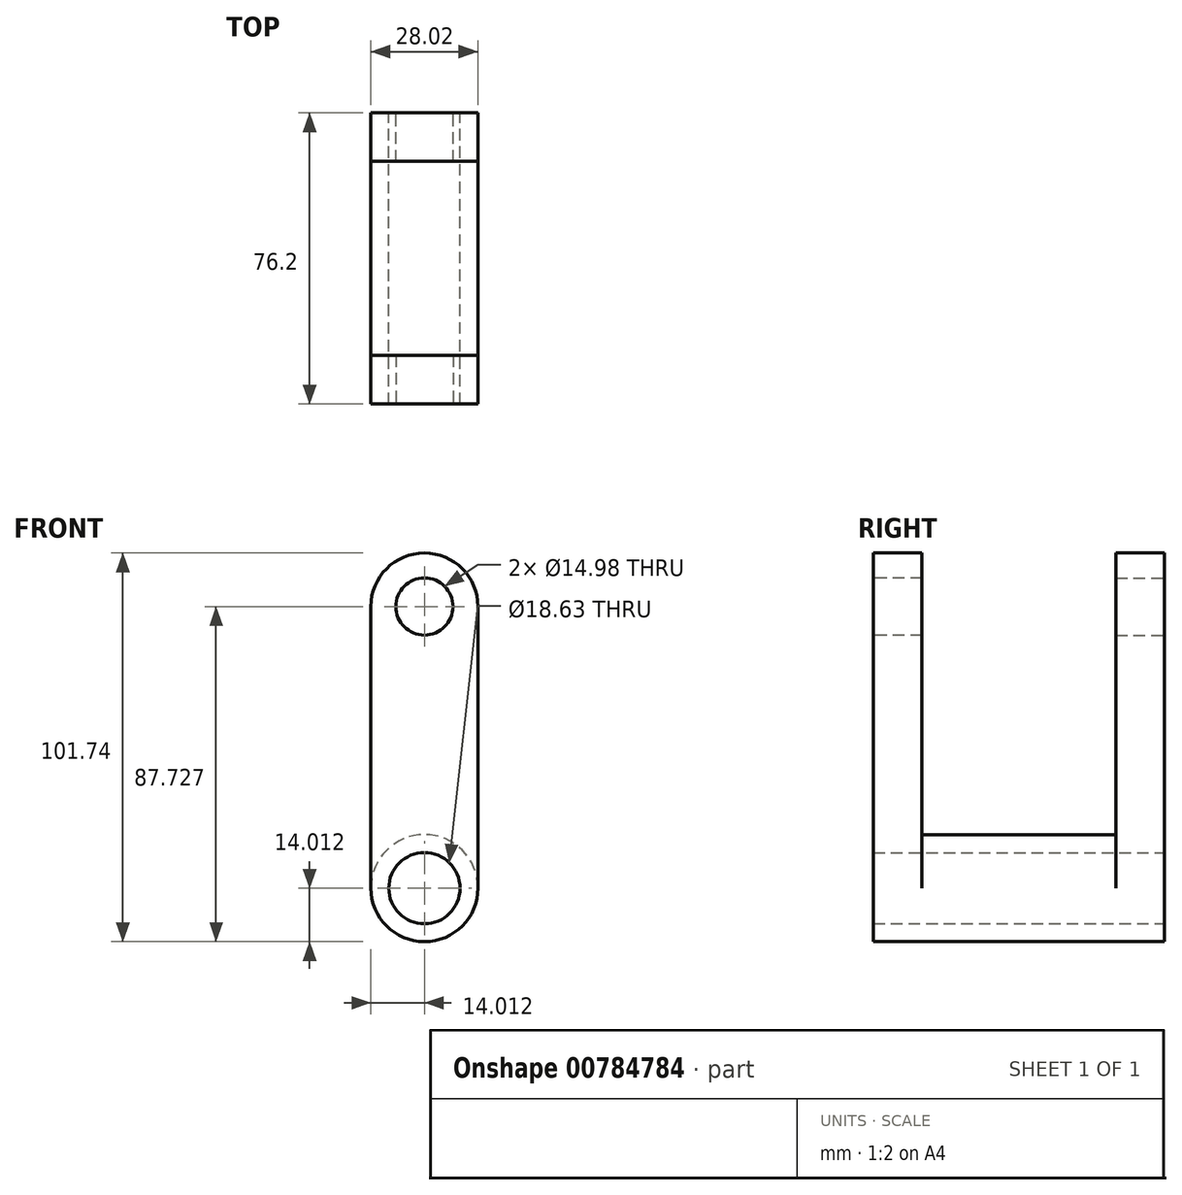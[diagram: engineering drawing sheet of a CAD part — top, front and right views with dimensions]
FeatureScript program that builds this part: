
annotation { "Feature Type Name" : "Feature", "Feature Type Description" : "" }
export const myFeature = defineFeature(function(context is Context, id is Id, definition is map)
    precondition{}
    {
        {
            var Q0;
            Q0=qCreatedBy(makeId("Front.planeOp"),FACE);
            var sketch = newSketch(context, id + "F0", { "sketchPlane" : qUnion([Q0])});
            skLineSegment(sketch, "E0.bottom", {"start": v(-35.03, 44.78) * mm, "end": v(-7, 44.78) * mm});
            skLineSegment(sketch, "E0.top", {"start": v(-35.03, -28.94) * mm, "end": v(-7, -28.94) * mm});
            skLineSegment(sketch, "E0.left", {"start": v(-35.03, 44.78) * mm, "end": v(-35.03, -28.94) * mm});
            skLineSegment(sketch, "E0.right", {"start": v(-7, 44.78) * mm, "end": v(-7, -28.94) * mm});
            skArc(sketch, "E1", {"start": v(-7, 44.78) * mm, "mid": v(-21.02, 58.79) * mm, "end": v(-35.03, 44.78) * mm});
            skArc(sketch, "E2", {"start": v(-35.03, -28.94) * mm, "mid": v(-21.02, -42.95) * mm, "end": v(-7, -28.94) * mm});
            skCircle(sketch, "E3", {"center": v(-21.02, -28.94) * mm, "radius": 9.32 * mm});
            skCircle(sketch, "E4", {"center": v(-21.02, 44.78) * mm, "radius": 7.49 * mm});
            skSolve(sketch);
        }
        {
            var Q0;
            Q0 = qSketchRegion(id + "F0", true);
            extrude(context, id + "F1", {"entities" : qUnion([Q0]), "depth" : 12.7 * mm, "offsetDistance" : 25.4 * mm});
        }
        {
            var Q0;
            Q0=makeQuery(id+"F1.opExtrude","CAP_FACE",FACE,{"disambiguationData":[OSD([sQuery(id+"F0.wireOp",EDGE,"E0.left"),sQuery(id+"F0.wireOp",EDGE,"E0.right"),sQuery(id+"F0.wireOp",EDGE,"E1"),sQuery(id+"F0.wireOp",EDGE,"E2"),sQuery(id+"F0.wireOp",EDGE,"E3"),sQuery(id+"F0.wireOp",EDGE,"E4")])],"isStart":false});
            var sketch = newSketch(context, id + "F2", { "sketchPlane" : qUnion([Q0])});
            skArc(sketch, "E5", {"start": v(-7, -28.94) * mm, "mid": v(-21.02, -14.93) * mm, "end": v(-35.03, -28.94) * mm});
            skSolve(sketch);
        }
        {
            var Q0;
            Q0 = qSketchRegion(id + "F2", true);
            var Q1;
            Q1=makeQuery(id+"F2.imprint","IMPRINT",FACE,{"disambiguationData":[TD([[makeQuery(id+"F2.imprint","IMPRINT",EDGE,{"derivedFrom":sQuery(id+"F2.wireOp",EDGE,"E5")}),1.0]])]});
            extrude(context, id + "F3", {"entities" : qUnion([Q0, Q1]), "operationType" : NewBodyOperationType.ADD, "depth" : 25.4 * mm, "offsetDistance" : 25.4 * mm});
        }
        {
            var Q0;
            Q0=makeQuery(id+"F1.opExtrude","SWEPT_BODY",BODY,{"disambiguationData":[OSD([sQuery(id+"F0.wireOp",EDGE,"E0.left"),sQuery(id+"F0.wireOp",EDGE,"E0.right"),sQuery(id+"F0.wireOp",EDGE,"E1"),sQuery(id+"F0.wireOp",EDGE,"E2"),sQuery(id+"F0.wireOp",EDGE,"E3"),sQuery(id+"F0.wireOp",EDGE,"E4")])]});
            var Q1;
            Q1=makeQuery(id+"F3.opExtrude","CAP_FACE",FACE,{"disambiguationData":[OSD([sQuery(id+"F0.wireOp",EDGE,"E2"),sQuery(id+"F0.wireOp",EDGE,"E3"),sQuery(id+"F2.wireOp",EDGE,"E5")])],"isStart":false});
            mirror(context, id + "F4", {"operationType" : NewBodyOperationType.ADD, "entities" : qUnion([Q0]), "mirrorPlane" : qUnion([Q1])});
        }
    });
